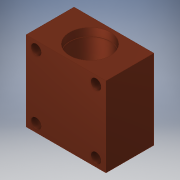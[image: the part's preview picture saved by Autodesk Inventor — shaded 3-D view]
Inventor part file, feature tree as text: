
AUTODESK INVENTOR PART (.ipt)
format: ipt  version: 2018 (Build 220112000, 112)  size: 154,112 bytes
history: native  units: in
note: dims shown in document units (in); Inventor stores cm internally (conversion verified against a paired STEP export)
features: sketch x7, extrude x5, hole x2
ambient origin geometry x8: Origin, YZ Plane, XZ Plane, XY Plane, X Axis, Y Axis, Z Axis, Center Point
bodies: Solid1 (feature_tree)
feature tree (14):
  extrude  "Extrusion1"  Depth=1.0in TaperAngle=0.0deg
  sketch  "Sketch2"  dims[d3=0.25in d6=0.501in]
  hole  "Hole1"  [1 undecoded]
  extrude  "Extrusion3"  Depth=0.46in TaperAngle=0.0deg
  extrude  "Extrusion4"  Depth=0.1in TaperAngle=0.0deg
  extrude  "Extrusion5"  Depth=1.0in
  extrude  "Extrusion6"  Depth=0.6in
  hole  "Hole2"  [1 undecoded]
  sketch  "Sketch1"  dims[d0=0.6in d1=1.0in d2=0.0in]
  sketch  "Sketch3"  dims[d7=0.46in d8=0.0in d9=0.501in d11=0.0in d12=0.46in]
  sketch  "Sketch5"  dims[d16=0.51in d18=0.0in d19=0.1in]
  sketch  "Sketch7"  dims[d28=180.0deg d29=0.6in d30=0.75in d31=0.8in d32=0.129in d33=0.224in d34=0.375in d35=0.25in d36=0.5635in d37=0.349in d38=0.8108in]
  sketch  "Sketch4"  dims[d13=0.51in d14=0.1in d15=0.0in]
  sketch  "Sketch6"  dims[d20=0.412in d21=0.866in d22=0.375in d23=0.25in d24=0.5635in d25=0.976in d26=0.8108in d27=1.0in]
note: 2 required parameter values undecoded (feature->parameter linkage not recoverable at this tier; creation-order binding heuristic only, values carry confidence <= 0.55)
